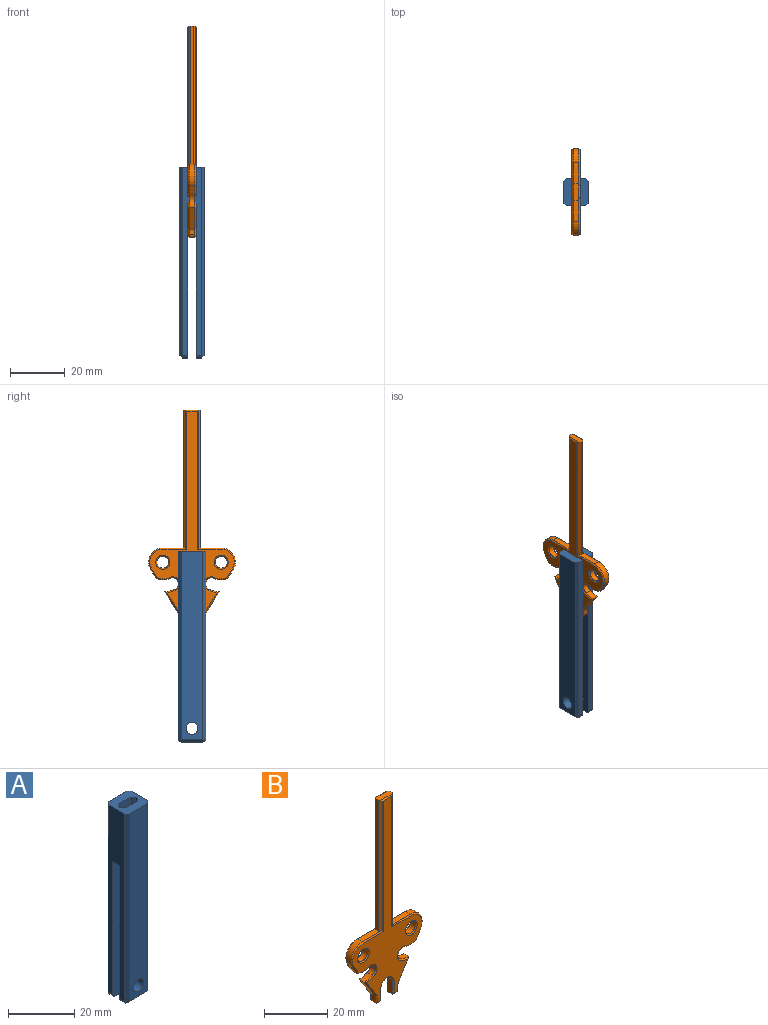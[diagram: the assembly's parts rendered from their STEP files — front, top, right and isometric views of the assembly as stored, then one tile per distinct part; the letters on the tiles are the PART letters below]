
ASSEMBLY  parts=2 mates=1
PART A: 33 faces, bbox 10x9x70 mm
  f0: plane 8x2mm, normal (0,0,-1), area 16mm2, adj f8,f9,f16,f28
  f1: plane 69x7mm, normal (-1,0,0), area 336mm2, adj f2,f4,f8,f15,f16,f18,f19,f24
  f2: cylinder r=1mm len=2mm, axis (0,1,0), area 3.1mm2, adj f1,f5,f15,f21
  f3: cylinder r=1mm len=2mm, axis (0,1,0), area 3.1mm2, adj f5,f7,f15,f22
  f4: plane 10x9mm, normal (0,0,1), area 69mm2, adj f1,f7,f11,f12,f13,f14,f15,f16
  f5: plane 8x2mm, normal (0,0,-1), area 16mm2, adj f2,f3,f15,f23
  f6: cylinder r=2.2mm len=4.4mm, axis (0,1,0), area 41.5mm2, adj f12,f15
  f7: plane 69x7mm, normal (1,0,0), area 336mm2, adj f3,f4,f9,f15,f16,f17,f20,f25
  f8: cylinder r=1mm len=2mm, axis (0,1,0), area 3.1mm2, adj f0,f1,f16,f26
  f9: cylinder r=1mm len=2mm, axis (0,1,0), area 3.1mm2, adj f0,f7,f16,f27
  f10: cylinder r=2.2mm len=4.4mm, axis (0,1,0), area 41.5mm2, adj f11,f16
  f11: plane 69x8mm, normal (0,-1,0), area 536.8mm2, adj f4,f10,f24,f25,f28
  f12: plane 69x8mm, normal (0,1,0), area 536.8mm2, adj f4,f6,f19,f20,f23
  f13: plane 20x1mm, normal (-1,0,0), area 20mm2, adj f4,f17,f30,f31
  f14: plane 20x1mm, normal (1,0,0), area 20mm2, adj f4,f18,f29,f32
  f15: plane 70x10mm, normal (0,-1,0), area 584.4mm2, adj f1,f2,f3,f4,f5,f6,f7,f17
  f16: plane 70x10mm, normal (0,1,0), area 584.4mm2, adj f0,f1,f4,f7,f8,f9,f10,f17
  f17: plane 3x2.5mm, normal (0,0,-1), area 5.5mm2, adj f7,f13,f15,f16,f30,f31
  f18: plane 3x2.5mm, normal (0,0,-1), area 5.5mm2, adj f1,f14,f15,f16,f29,f32
  f19: plane 69x1mm, normal (-0.71,0.71,0), area 97.6mm2, adj f1,f4,f12,f21
  f20: plane 69x1mm, normal (0.71,0.71,0), area 97.6mm2, adj f4,f7,f12,f22
  f21: cone r=1mm half-angle=45deg, axis (0,-1,0), area 1.1mm2, adj f2,f19,f23
  f22: cone r=1mm half-angle=45deg, axis (0,-1,0), area 1.1mm2, adj f3,f20,f23
  f23: plane 8x1mm, normal (0,0.71,-0.71), area 11.3mm2, adj f5,f12,f21,f22
  f24: plane 69x1mm, normal (-0.71,-0.71,0), area 97.6mm2, adj f1,f4,f11,f26
  f25: plane 69x1mm, normal (0.71,-0.71,0), area 97.6mm2, adj f4,f7,f11,f27
  f26: cone r=1mm half-angle=45deg, axis (0,1,0), area 1.1mm2, adj f8,f24,f28
  f27: cone r=1mm half-angle=45deg, axis (0,1,0), area 1.1mm2, adj f9,f25,f28
  f28: plane 8x1mm, normal (0,-0.71,-0.71), area 11.3mm2, adj f0,f11,f26,f27
  f29: plane 20x1mm, normal (0.71,0.71,0), area 28.3mm2, adj f4,f14,f16,f18
  f30: plane 20x1mm, normal (-0.71,0.71,0), area 28.3mm2, adj f4,f13,f16,f17
  f31: plane 20x1mm, normal (-0.71,-0.71,0), area 28.3mm2, adj f4,f13,f15,f17
  f32: plane 20x1mm, normal (0.71,-0.71,0), area 28.3mm2, adj f4,f14,f15,f18
PART B: 90 faces, bbox 31.8x3x77.6 mm
  f0: plane 6.2x2.2mm, normal (0,0,1), area 12.9mm2, adj f1,f17,f30,f31,f32,f33,f56,f84
  f1: plane 50.64x1mm, normal (-1,0,0), area 50.6mm2, adj f0,f2,f31,f32
  f2: plane 8.2x2.2mm, normal (0,0,1), area 17.1mm2, adj f1,f3,f31,f32,f52,f80
  f3: cylinder r=5.2mm len=7.98mm, axis (0,1,0), area 24.4mm2, adj f2,f4,f50,f78
  f4: plane 3.29x2.2mm, normal (-0.85,0,-0.53), area 8.6mm2, adj f3,f5,f48,f76
  f5: cylinder r=6.49mm len=4.93mm, axis (0,1,0), area 11.1mm2, adj f4,f6,f46,f74
  f6: cylinder r=2.2mm len=4.21mm, axis (0,1,0), area 15.2mm2, adj f5,f7,f44,f72
  f7: cylinder r=10.89mm len=3.66mm, axis (0,1,0), area 8.3mm2, adj f6,f8,f42,f70
  f8: plane 7.87x4.98mm, normal (-0.85,0,-0.53), area 20.5mm2, adj f7,f9,f40,f68
  f9: plane 2.2x2mm, normal (-1,0,0), area 4.4mm2, adj f8,f10,f38,f66
  f10: cylinder r=1mm len=2.2mm, axis (0,1,0), area 3.5mm2, adj f9,f11,f36,f64
  f11: plane 2.2x1.4mm, normal (0,0,-1), area 3.1mm2, adj f10,f12,f34,f62
  f12: plane 5x2.2mm, normal (1,0,0), area 11mm2, adj f11,f13,f35,f63
  f13: cylinder r=2.6mm len=5.2mm, axis (0,1,0), area 18mm2, adj f12,f28,f37,f65
  f14: cylinder r=2.2mm len=4.4mm, axis (0,1,0), area 30.4mm2, adj f61,f89
  f15: plane 76.79x31mm, normal (0,-1,0), area 603.6mm2, adj f34,f35,f36,f37,f38,f39,f40,f41
  f16: plane 76.79x31mm, normal (0,1,0), area 603.6mm2, adj f62,f63,f64,f65,f66,f67,f68,f69
  f17: plane 50.64x1mm, normal (1,0,0), area 50.6mm2, adj f0,f18,f30,f33
  f18: plane 8.2x2.2mm, normal (0,0,1), area 17.1mm2, adj f17,f19,f30,f33,f59,f87
  f19: cylinder r=5.2mm len=7.98mm, axis (0,1,0), area 24.4mm2, adj f18,f20,f57,f85
  f20: plane 3.29x2.2mm, normal (0.85,0,-0.53), area 8.6mm2, adj f19,f21,f55,f83
  f21: cylinder r=6.49mm len=4.93mm, axis (0,1,0), area 11.1mm2, adj f20,f22,f53,f81
  f22: cylinder r=2.2mm len=4.21mm, axis (0,1,0), area 15.2mm2, adj f21,f23,f51,f79
  f23: cylinder r=10.89mm len=3.66mm, axis (0,1,0), area 8.3mm2, adj f22,f24,f49,f77
  f24: plane 7.87x4.98mm, normal (0.85,0,-0.53), area 20.5mm2, adj f23,f25,f47,f75
  f25: plane 2.2x2mm, normal (1,0,0), area 4.4mm2, adj f24,f26,f45,f73
  f26: cylinder r=1mm len=2.2mm, axis (0,1,0), area 3.5mm2, adj f25,f27,f43,f71
  f27: plane 2.2x1.4mm, normal (0,0,-1), area 3.1mm2, adj f26,f28,f41,f69
  f28: plane 5x2.2mm, normal (-1,0,0), area 11mm2, adj f13,f27,f39,f67
  f29: cylinder r=2.2mm len=4.4mm, axis (0,1,0), area 30.4mm2, adj f60,f88
  f30: plane 50.92x0.88mm, normal (0.71,0.71,0), area 63.2mm2, adj f0,f17,f18,f84,f86,f87
  f31: plane 50.92x0.88mm, normal (-0.71,0.71,0), area 63.2mm2, adj f0,f1,f2,f80,f82,f84
  f32: plane 50.92x0.88mm, normal (-0.71,-0.71,0), area 63.2mm2, adj f0,f1,f2,f52,f54,f56
  f33: plane 50.92x0.88mm, normal (0.71,-0.71,0), area 63.2mm2, adj f0,f17,f18,f56,f58,f59
  f34: plane 1.4x0.4mm, normal (0,-0.71,-0.71), area 0.7mm2, adj f11,f15,f35,f36
  f35: plane 5x0.4mm, normal (0.71,-0.71,0), area 2.7mm2, adj f12,f15,f34,f37
  f36: cone r=0.6mm half-angle=45deg, axis (0,1,0), area 0.7mm2, adj f10,f15,f34,f38
  f37: cone r=2.6mm half-angle=45deg, axis (0,-1,0), area 5mm2, adj f13,f15,f35,f39
  f38: plane 2.12x0.4mm, normal (-0.71,-0.71,0), area 1.2mm2, adj f9,f15,f36,f40
  f39: plane 5x0.4mm, normal (-0.71,-0.71,0), area 2.7mm2, adj f15,f28,f37,f41
  f40: plane 7.88x5.39mm, normal (-0.6,-0.71,-0.38), area 5.1mm2, adj f8,f15,f38,f42
  f41: plane 1.4x0.4mm, normal (0,-0.71,-0.71), area 0.7mm2, adj f15,f27,f39,f43
  f42: cone r=10.89mm half-angle=45deg, axis (0,-1,0), area 2mm2, adj f7,f15,f40,f44
  f43: cone r=1mm half-angle=45deg, axis (0,1,0), area 0.7mm2, adj f15,f26,f41,f45
  f44: cone r=2.2mm half-angle=45deg, axis (0,-1,0), area 4.3mm2, adj f6,f15,f42,f46
  f45: plane 2.12x0.4mm, normal (0.71,-0.71,0), area 1.2mm2, adj f15,f25,f43,f47
  f46: cone r=6.09mm half-angle=45deg, axis (0,1,0), area 2.7mm2, adj f5,f15,f44,f48
  f47: plane 7.88x5.39mm, normal (0.6,-0.71,-0.38), area 5.1mm2, adj f15,f24,f45,f49
  f48: plane 3.5x2.35mm, normal (-0.6,-0.71,-0.38), area 2.2mm2, adj f4,f15,f46,f50
  f49: cone r=11.29mm half-angle=45deg, axis (0,-1,0), area 2mm2, adj f15,f23,f47,f51
  f50: cone r=5.2mm half-angle=45deg, axis (0,1,0), area 6mm2, adj f3,f15,f48,f52
  f51: cone r=2.6mm half-angle=45deg, axis (0,-1,0), area 4.3mm2, adj f15,f22,f49,f53
  f52: plane 8.77x0.4mm, normal (0,-0.71,0.71), area 4.8mm2, adj f2,f15,f32,f50,f54
  f53: cone r=6.49mm half-angle=45deg, axis (0,1,0), area 2.7mm2, adj f15,f21,f51,f55
  f54: plane 50.75x0.28mm, normal (-0.38,-0.92,0), area 15.5mm2, adj f15,f32,f52,f56
  f55: plane 3.5x2.35mm, normal (0.6,-0.71,-0.38), area 2.2mm2, adj f15,f20,f53,f57
  f56: plane 5x0.4mm, normal (0,-0.71,0.71), area 2.6mm2, adj f0,f15,f32,f33,f54,f58
  f57: cone r=4.8mm half-angle=45deg, axis (0,1,0), area 6mm2, adj f15,f19,f55,f59
  f58: plane 50.75x0.28mm, normal (0.38,-0.92,0), area 15.5mm2, adj f15,f33,f56,f59
  f59: plane 8.77x0.4mm, normal (0,-0.71,0.71), area 4.8mm2, adj f15,f18,f33,f57,f58
  f60: cone r=2.6mm half-angle=45deg, axis (0,-1,0), area 8.5mm2, adj f15,f29
  f61: cone r=2.2mm half-angle=45deg, axis (0,-1,0), area 8.5mm2, adj f14,f15
  f62: plane 1.4x0.4mm, normal (0,0.71,-0.71), area 0.7mm2, adj f11,f16,f63,f64
  f63: plane 5x0.4mm, normal (0.71,0.71,0), area 2.7mm2, adj f12,f16,f62,f65
  f64: cone r=1mm half-angle=45deg, axis (0,-1,0), area 0.7mm2, adj f10,f16,f62,f66
  f65: cone r=3mm half-angle=45deg, axis (0,1,0), area 5mm2, adj f13,f16,f63,f67
  f66: plane 2.12x0.4mm, normal (-0.71,0.71,0), area 1.2mm2, adj f9,f16,f64,f68
  f67: plane 5x0.4mm, normal (-0.71,0.71,0), area 2.7mm2, adj f16,f28,f65,f69
  f68: plane 7.88x5.39mm, normal (-0.6,0.71,-0.38), area 5.1mm2, adj f8,f16,f66,f70
  f69: plane 1.4x0.4mm, normal (0,0.71,-0.71), area 0.7mm2, adj f16,f27,f67,f71
  f70: cone r=11.29mm half-angle=45deg, axis (0,1,0), area 2mm2, adj f7,f16,f68,f72
  f71: cone r=0.6mm half-angle=45deg, axis (0,-1,0), area 0.7mm2, adj f16,f26,f69,f73
  f72: cone r=2.6mm half-angle=45deg, axis (0,1,0), area 4.3mm2, adj f6,f16,f70,f74
  f73: plane 2.12x0.4mm, normal (0.71,0.71,0), area 1.2mm2, adj f16,f25,f71,f75
  f74: cone r=6.49mm half-angle=45deg, axis (0,-1,0), area 2.7mm2, adj f5,f16,f72,f76
  f75: plane 7.88x5.39mm, normal (0.6,0.71,-0.38), area 5.1mm2, adj f16,f24,f73,f77
  f76: plane 3.5x2.35mm, normal (-0.6,0.71,-0.38), area 2.2mm2, adj f4,f16,f74,f78
  f77: cone r=10.89mm half-angle=45deg, axis (0,1,0), area 2mm2, adj f16,f23,f75,f79
  f78: cone r=4.8mm half-angle=45deg, axis (0,-1,0), area 6mm2, adj f3,f16,f76,f80
  f79: cone r=2.2mm half-angle=45deg, axis (0,1,0), area 4.3mm2, adj f16,f22,f77,f81
  f80: plane 8.77x0.4mm, normal (0,0.71,0.71), area 4.8mm2, adj f2,f16,f31,f78,f82
  f81: cone r=6.09mm half-angle=45deg, axis (0,-1,0), area 2.7mm2, adj f16,f21,f79,f83
  f82: plane 50.75x0.28mm, normal (-0.38,0.92,0), area 15.5mm2, adj f16,f31,f80,f84
  f83: plane 3.5x2.35mm, normal (0.6,0.71,-0.38), area 2.2mm2, adj f16,f20,f81,f85
  f84: plane 5x0.4mm, normal (0,0.71,0.71), area 2.6mm2, adj f0,f16,f30,f31,f82,f86
  f85: cone r=5.2mm half-angle=45deg, axis (0,-1,0), area 6mm2, adj f16,f19,f83,f87
  f86: plane 50.75x0.28mm, normal (0.38,0.92,0), area 15.5mm2, adj f16,f30,f84,f87
  f87: plane 8.77x0.4mm, normal (0,0.71,0.71), area 4.8mm2, adj f16,f18,f30,f85,f86
  f88: cone r=2.2mm half-angle=45deg, axis (0,1,0), area 8.5mm2, adj f16,f29
  f89: cone r=2.6mm half-angle=45deg, axis (0,1,0), area 8.5mm2, adj f14,f16
PLACE A rot(axis=(0,0,-1),90deg) t=(21.5,0,-5)mm fixed
PLACE B rot(axis=(0,0,-1),90deg) t=(27.5,0,39.23)mm
MATE slider B.f11 <-> A.f0  axis (0,0,1) through (0,0,44.23)mm
